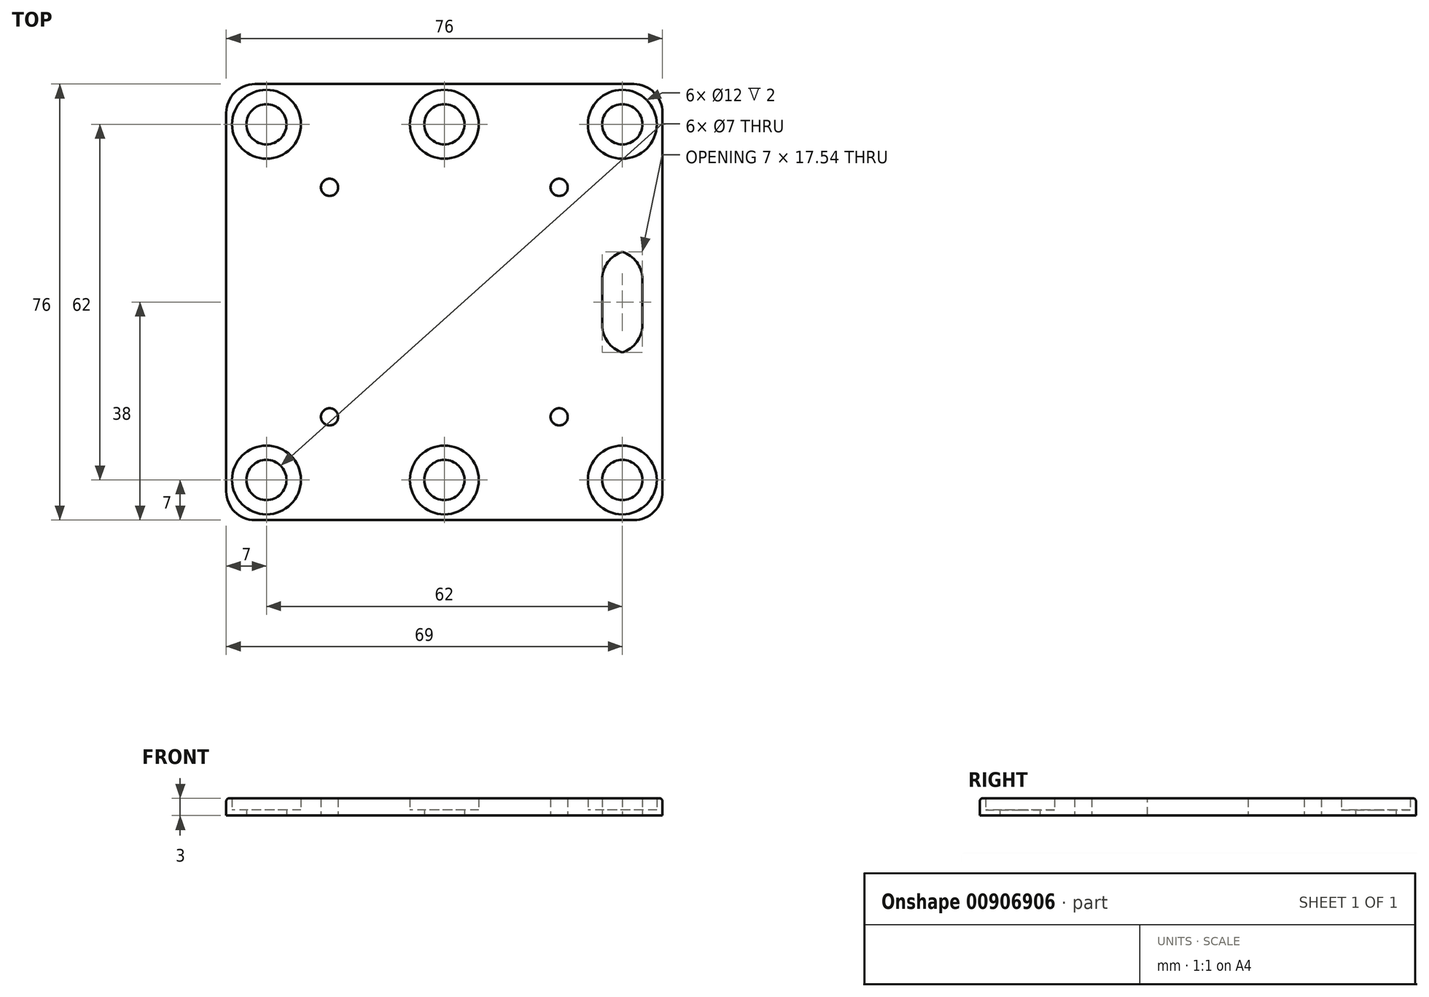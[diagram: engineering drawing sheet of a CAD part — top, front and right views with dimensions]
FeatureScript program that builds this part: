
annotation { "Feature Type Name" : "Feature", "Feature Type Description" : "" }
export const myFeature = defineFeature(function(context is Context, id is Id, definition is map)
    precondition{}
    {
        {
            var Q0;
            Q0=qCreatedBy(makeId("Top.planeOp"),FACE);
            var sketch = newSketch(context, id + "F0", { "sketchPlane" : qUnion([Q0])});
            skLineSegment(sketch, "E0.bottom", {"start": v(38, -38) * mm, "end": v(-38, -38) * mm});
            skLineSegment(sketch, "E0.top", {"start": v(38, 38) * mm, "end": v(-38, 38) * mm});
            skLineSegment(sketch, "E0.left", {"start": v(38, -38) * mm, "end": v(38, 38) * mm});
            skLineSegment(sketch, "E0.right", {"start": v(-38, -38) * mm, "end": v(-38, 38) * mm});
            skCircle(sketch, "E1", {"center": v(-31, 31) * mm, "radius": 3.5 * mm});
            skCircle(sketch, "E2", {"center": v(31, 31) * mm, "radius": 3.5 * mm});
            skCircle(sketch, "E3", {"center": v(31, -31) * mm, "radius": 3.5 * mm});
            skCircle(sketch, "E4", {"center": v(-31, -31) * mm, "radius": 3.5 * mm});
            skCircle(sketch, "E5", {"center": v(-31, 31) * mm, "radius": 6 * mm});
            skCircle(sketch, "E6", {"center": v(31, 31) * mm, "radius": 6 * mm});
            skCircle(sketch, "E7", {"center": v(31, -31) * mm, "radius": 6 * mm});
            skCircle(sketch, "E8", {"center": v(-31, -31) * mm, "radius": 6 * mm});
            skPoint(sketch, "E9.middle", {"position": v(0, 0) * mm});
            skCircle(sketch, "E10", {"center": v(-20, -20) * mm, "radius": 1.5 * mm});
            skCircle(sketch, "E11", {"center": v(-20, 20) * mm, "radius": 1.5 * mm});
            skCircle(sketch, "E12", {"center": v(20, 20) * mm, "radius": 1.5 * mm});
            skCircle(sketch, "E13", {"center": v(20, -20) * mm, "radius": 1.5 * mm});
            skLineSegment(sketch, "E14.bottom", {"start": v(27.5, -9) * mm, "end": v(34.5, -9) * mm});
            skLineSegment(sketch, "E14.top", {"start": v(27.5, 9) * mm, "end": v(34.5, 9) * mm});
            skLineSegment(sketch, "E14.left", {"start": v(27.5, -9) * mm, "end": v(27.5, 9) * mm});
            skLineSegment(sketch, "E14.right", {"start": v(34.5, -9) * mm, "end": v(34.5, 9) * mm});
            skPoint(sketch, "E14.middle", {"position": v(31, 0) * mm});
            skCircle(sketch, "E15", {"center": v(0, 31) * mm, "radius": 3.5 * mm});
            skCircle(sketch, "E16", {"center": v(0, 31) * mm, "radius": 6 * mm});
            skCircle(sketch, "E17", {"center": v(0, -31) * mm, "radius": 3.5 * mm});
            skCircle(sketch, "E18", {"center": v(0, -31) * mm, "radius": 6 * mm});
            skSolve(sketch);
        }
        {
            var Q0;
            Q0=makeQuery(id+"F0.imprint","IMPRINT",FACE,{"disambiguationData":[TD([[makeQuery(id+"F0.imprint","IMPRINT",EDGE,{"derivedFrom":sQuery(id+"F0.wireOp",EDGE,"E0.bottom")}),-1.0]])]});
            extrude(context, id + "F1", {"entities" : qUnion([Q0]), "depth" : 3 * mm, "offsetDistance" : 25 * mm});
        }
        {
            var Q0;
            Q0=makeQuery(id+"F0.imprint","IMPRINT",FACE,{"disambiguationData":[TD([[makeQuery(id+"F0.imprint","IMPRINT",EDGE,{"derivedFrom":sQuery(id+"F0.wireOp",EDGE,"E1")}),-1.0]])]});
            var Q1;
            Q1=makeQuery(id+"F0.imprint","IMPRINT",FACE,{"disambiguationData":[TD([[makeQuery(id+"F0.imprint","IMPRINT",EDGE,{"derivedFrom":sQuery(id+"F0.wireOp",EDGE,"E2")}),-1.0]])]});
            var Q2;
            Q2=makeQuery(id+"F0.imprint","IMPRINT",FACE,{"disambiguationData":[TD([[makeQuery(id+"F0.imprint","IMPRINT",EDGE,{"derivedFrom":sQuery(id+"F0.wireOp",EDGE,"E3")}),-1.0]])]});
            var Q3;
            Q3=makeQuery(id+"F0.imprint","IMPRINT",FACE,{"disambiguationData":[TD([[makeQuery(id+"F0.imprint","IMPRINT",EDGE,{"derivedFrom":sQuery(id+"F0.wireOp",EDGE,"E4")}),-1.0]])]});
            var Q4;
            {var subQ0=sQuery(id+"F0.wireOp",EDGE,"E18");var subQ1=sQuery(id+"F0.wireOp",EDGE,"TDfoTxur-vch8-KdUk-5QRg-aoZRvWIfuVhj");var subQ2=makeQuery(id+"F0.imprint","INTERSECT",VERTEX,{"disambiguationData":[OD(0.0)],"derivedFrom":[subQ1,subQ0]});Q4=makeQuery(id+"F0.imprint","IMPRINT",FACE,{"disambiguationData":[TD([[makeQuery(id+"F0.imprint","IMPRINT",EDGE,{"disambiguationData":[TD([[subQ2,-1.0]])],"derivedFrom":subQ1}),-1.0]])]});}
            var Q5;
            {var subQ0=sQuery(id+"F0.wireOp",EDGE,"E18");var subQ1=sQuery(id+"F0.wireOp",EDGE,"TDfoTxur-vch8-KdUk-5QRg-aoZRvWIfuVhj");var subQ2=makeQuery(id+"F0.imprint","INTERSECT",VERTEX,{"disambiguationData":[OD(0.0)],"derivedFrom":[subQ1,subQ0]});Q5=makeQuery(id+"F0.imprint","IMPRINT",FACE,{"disambiguationData":[TD([[makeQuery(id+"F0.imprint","IMPRINT",EDGE,{"disambiguationData":[TD([[subQ2,-1.0]])],"derivedFrom":subQ1}),1.0]])]});}
            var Q6;
            {var subQ0=sQuery(id+"F0.wireOp",EDGE,"E16");var subQ1=sQuery(id+"F0.wireOp",EDGE,"FbiM7Lmk-G9Xb-La2m-5xM5-oXfNYEcgzxL4");var subQ2=makeQuery(id+"F0.imprint","INTERSECT",VERTEX,{"disambiguationData":[OD(0.0)],"derivedFrom":[subQ1,subQ0]});Q6=makeQuery(id+"F0.imprint","IMPRINT",FACE,{"disambiguationData":[TD([[makeQuery(id+"F0.imprint","IMPRINT",EDGE,{"disambiguationData":[TD([[subQ2,-1.0]])],"derivedFrom":subQ1}),-1.0]])]});}
            var Q7;
            {var subQ0=sQuery(id+"F0.wireOp",EDGE,"E16");var subQ1=sQuery(id+"F0.wireOp",EDGE,"FbiM7Lmk-G9Xb-La2m-5xM5-oXfNYEcgzxL4");var subQ2=makeQuery(id+"F0.imprint","INTERSECT",VERTEX,{"disambiguationData":[OD(0.0)],"derivedFrom":[subQ1,subQ0]});Q7=makeQuery(id+"F0.imprint","IMPRINT",FACE,{"disambiguationData":[TD([[makeQuery(id+"F0.imprint","IMPRINT",EDGE,{"disambiguationData":[TD([[subQ2,-1.0]])],"derivedFrom":subQ1}),1.0]])]});}
            var Q8;
            Q8=makeQuery(id+"F0.imprint","IMPRINT",FACE,{"disambiguationData":[TD([[makeQuery(id+"F0.imprint","IMPRINT",EDGE,{"derivedFrom":sQuery(id+"F0.wireOp",EDGE,"E15")}),-1.0]])]});
            var Q9;
            Q9=makeQuery(id+"F0.imprint","IMPRINT",FACE,{"disambiguationData":[TD([[makeQuery(id+"F0.imprint","IMPRINT",EDGE,{"derivedFrom":sQuery(id+"F0.wireOp",EDGE,"E17")}),-1.0]])]});
            extrude(context, id + "F2", {"entities" : qUnion([Q0, Q1, Q2, Q3, Q4, Q5, Q6, Q7, Q8, Q9]), "operationType" : NewBodyOperationType.ADD, "depth" : 1 * mm, "offsetDistance" : 25 * mm});
        }
        {
            var Q0;
            Q0=makeQuery(id+"F1.opExtrude","SWEPT_EDGE",EDGE,{"disambiguationData":[OSD([sQuery(id+"F0.wireOp",EDGE,"E0.bottom"),sQuery(id+"F0.wireOp",EDGE,"E0.right")])]});
            var Q1;
            Q1=makeQuery(id+"F1.opExtrude","SWEPT_EDGE",EDGE,{"disambiguationData":[OSD([sQuery(id+"F0.wireOp",EDGE,"E0.bottom"),sQuery(id+"F0.wireOp",EDGE,"E0.left")])]});
            var Q2;
            Q2=makeQuery(id+"F1.opExtrude","SWEPT_EDGE",EDGE,{"disambiguationData":[OSD([sQuery(id+"F0.wireOp",EDGE,"E0.top"),sQuery(id+"F0.wireOp",EDGE,"E0.left")])]});
            var Q3;
            Q3=makeQuery(id+"F1.opExtrude","SWEPT_EDGE",EDGE,{"disambiguationData":[OSD([sQuery(id+"F0.wireOp",EDGE,"E0.top"),sQuery(id+"F0.wireOp",EDGE,"E0.right")])]});
            var Q4;
            Q4=makeQuery(id+"F1.opExtrude","SWEPT_EDGE",EDGE,{"disambiguationData":[OSD([sQuery(id+"F0.wireOp",EDGE,"E14.top"),sQuery(id+"F0.wireOp",EDGE,"E14.right")])]});
            var Q5;
            Q5=makeQuery(id+"F1.opExtrude","SWEPT_EDGE",EDGE,{"disambiguationData":[OSD([sQuery(id+"F0.wireOp",EDGE,"E14.bottom"),sQuery(id+"F0.wireOp",EDGE,"E14.right")])]});
            var Q6;
            Q6=makeQuery(id+"F1.opExtrude","SWEPT_EDGE",EDGE,{"disambiguationData":[OSD([sQuery(id+"F0.wireOp",EDGE,"E14.bottom"),sQuery(id+"F0.wireOp",EDGE,"E14.left")])]});
            var Q7;
            Q7=makeQuery(id+"F1.opExtrude","SWEPT_EDGE",EDGE,{"disambiguationData":[OSD([sQuery(id+"F0.wireOp",EDGE,"E14.top"),sQuery(id+"F0.wireOp",EDGE,"E14.left")])]});
            fillet(context, id + "F3", {"entities" : qUnion([Q0, Q1, Q2, Q3, Q4, Q5, Q6, Q7]), "radius" : 5 * mm, "tangentPropagation" : true, "allowEdgeOverflow" : false});
        }
        {
            var Q0;
            Q0=makeQuery(id+"F1.opExtrude","CAP_EDGE",EDGE,{"disambiguationData":[OSD([sQuery(id+"F0.wireOp",EDGE,"E0.bottom")])],"isStart":false});
            fillet(context, id + "F4", {"entities" : qUnion([Q0]), "radius" : 0.5 * mm, "tangentPropagation" : true, "allowEdgeOverflow" : false});
        }
    });
